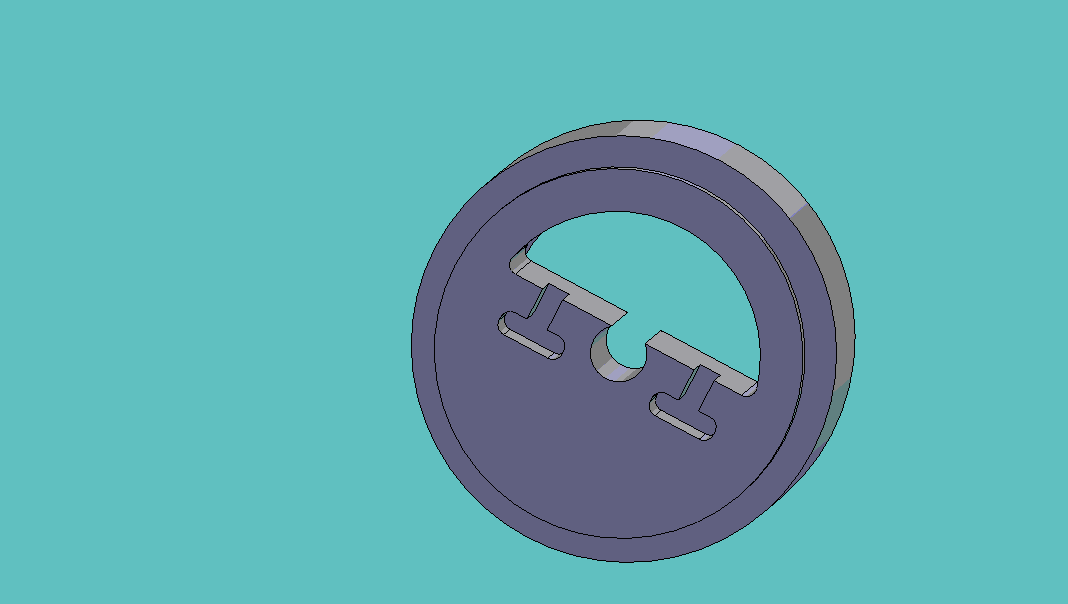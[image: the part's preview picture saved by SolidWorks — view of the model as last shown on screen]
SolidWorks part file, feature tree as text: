
SOLIDWORKS PART (.sldprt)
format: sldprt  version: not decoded by parser v0  size: 189,440 bytes
history: native  units: mm
features: plane x3, sketch x3, cut_extrude x2, material x1, revolve x1 (+11 scaffold rows collapsed)
feature tree (21):
  scaffold x11  (default folders/planes/origin — collapsed)
  material  "Matériau <non spécifié>"
  plane  "Plan de face"
  plane  "Plan de dessus"
  plane  "Plan de droite"
  sketch  "Esquisse1"  dims[c1.D1=4.0mm c1.D2=16.0mm c1.D3=6.0mm c1.D4=12.5mm c1.D5=15.0mm c1.D6=2.0mm c1.D7=2.4mm c1.D8=3.0mm c1.D9=6.4mm c1.D10=17.5mm c1.D11=6.4mm c1.D12=3.0mm c1.D13=2.4mm c1.D14=2.0mm c1.D15=22.0mm c1.D16=4.0mm c2.D5=15.0mm c2.D1=4.0mm]
  revolve  "Révolution1"  Angle=360deg
  sketch  "Esquisse2"  dims[D1=3.0mm]
  cut_extrude  "Extrusion1"  [1 undecoded]
  sketch  "Esquisse3"  dims[c1.D1=1.6mm c1.D2=1.6mm c1.D3=5.0mm c2.D1=3.5mm]
  cut_extrude  "Extrusion2"  Depth=6mm
decode coverage: 5 of 6 modeling features carry decoded parameters
note: 1 parameter value undecoded
note: suppression state not decoded; provenance and decode notes live in map.json
